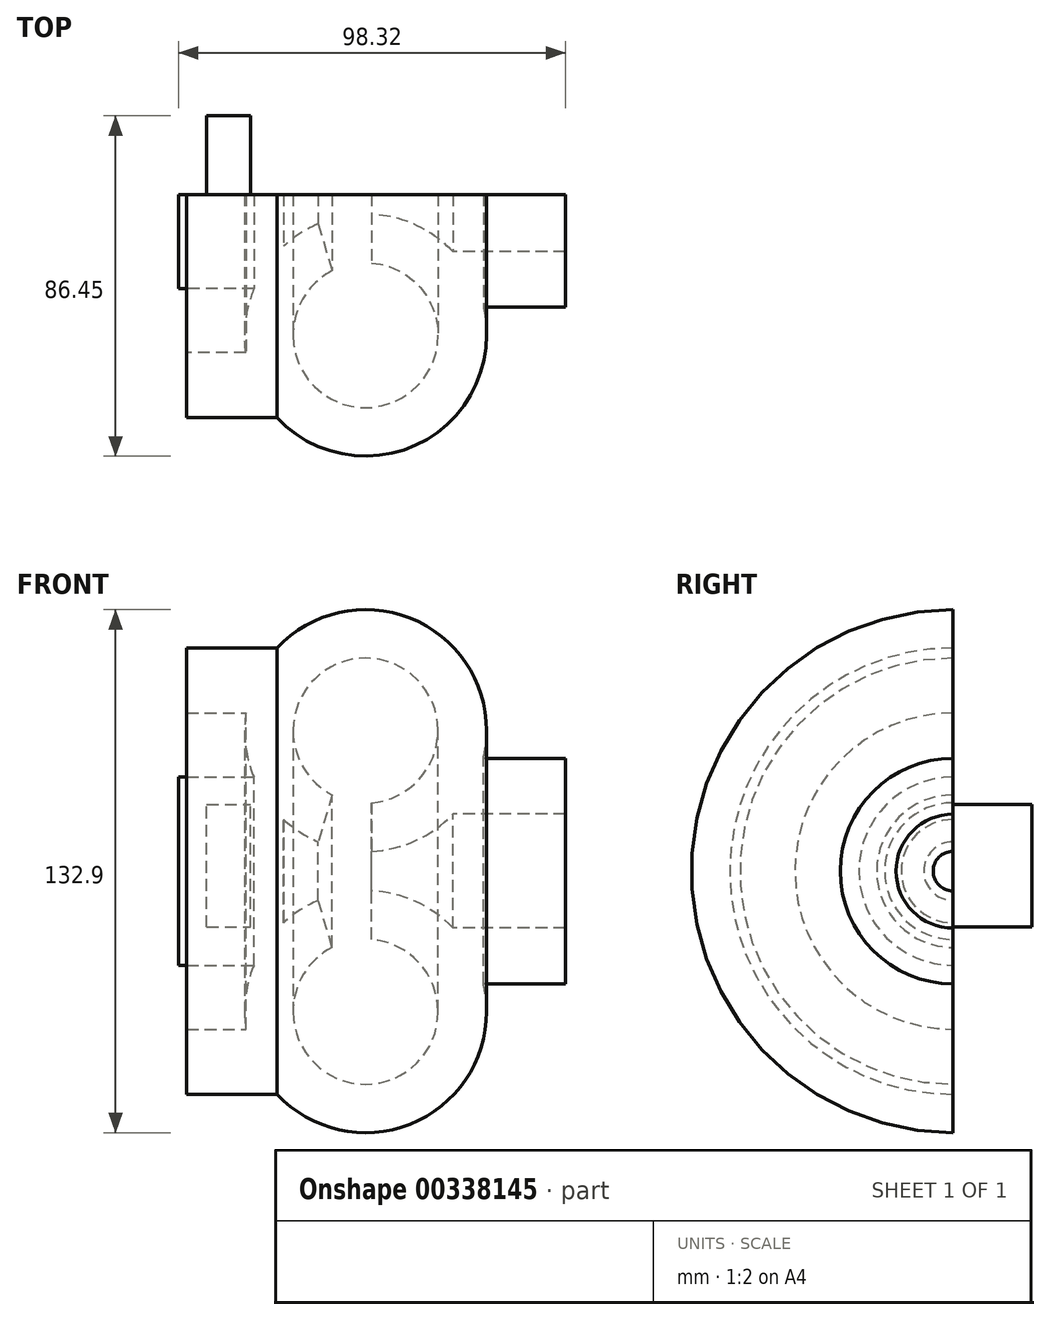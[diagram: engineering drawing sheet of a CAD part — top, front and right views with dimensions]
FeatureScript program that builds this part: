
annotation { "Feature Type Name" : "Feature", "Feature Type Description" : "" }
export const myFeature = defineFeature(function(context is Context, id is Id, definition is map)
    precondition{}
    {
        {
            var Q0;
            Q0=qCreatedBy(makeId("Front.planeOp"),FACE);
            var sketch = newSketch(context, id + "F0", { "sketchPlane" : qUnion([Q0])});
            skArc(sketch, "E0", {"start": v(-9.6, 40.15) * mm, "mid": v(-9.67, 31.9) * mm, "end": v(-7.55, 23.91) * mm});
            skLineSegment(sketch, "E1.bottom", {"start": v(71.6, 14.47) * mm, "end": v(43, 14.47) * mm});
            skLineSegment(sketch, "E1.top", {"start": v(71.6, 28.64) * mm, "end": v(50.71, 28.64) * mm});
            skLineSegment(sketch, "E1.left", {"start": v(71.6, 14.47) * mm, "end": v(71.6, 28.64) * mm});
            skLineSegment(sketch, "E2.bottom", {"start": v(-26.72, 0) * mm, "end": v(0, 0) * mm});
            skLineSegment(sketch, "E2.top", {"start": v(-26.72, 23.91) * mm, "end": v(-7.55, 23.91) * mm});
            skLineSegment(sketch, "E2.left", {"start": v(-26.72, 0) * mm, "end": v(-26.72, 23.91) * mm});
            skLineSegment(sketch, "E2.right", {"start": v(0, 0) * mm, "end": v(0, 13.12) * mm});
            skLineSegment(sketch, "E3.bottom", {"start": v(-24.65, 56.69) * mm, "end": v(-1.65, 56.69) * mm});
            skLineSegment(sketch, "E3.top", {"start": v(-24.65, 40.15) * mm, "end": v(-9.6, 40.15) * mm});
            skLineSegment(sketch, "E3.right", {"start": v(-24.65, 56.69) * mm, "end": v(-24.65, 40.15) * mm});
            skPoint(sketch, "E4.orphan", {"position": v(0, 56.69) * mm});
            skArc(sketch, "E5.trimOffspring", {"start": v(0, 13.12) * mm, "mid": v(4.15, 9.9) * mm, "end": v(8.8, 7.45) * mm});
            skPoint(sketch, "E6.orphan", {"position": v(0, 23.91) * mm});
            skArc(sketch, "E7.trimOffspring", {"start": v(50.71, 28.64) * mm, "mid": v(35.32, 62.81) * mm, "end": v(-1.65, 56.69) * mm});
            skArc(sketch, "E8", {"start": v(22.26, 17.36) * mm, "mid": v(24.48, 53.78) * mm, "end": v(12.33, 19.38) * mm});
            skLineSegment(sketch, "E9", {"start": v(22.26, 17.36) * mm, "end": v(22.26, 5.03) * mm});
            skLineSegment(sketch, "E10", {"start": v(12.33, 19.38) * mm, "end": v(8.8, 7.45) * mm});
            skArc(sketch, "E11.trimOffspring", {"start": v(22.26, 5.03) * mm, "mid": v(33.54, 7.75) * mm, "end": v(43, 14.47) * mm});
            skSolve(sketch);
        }
        {
            var Q0;
            Q0=makeQuery(id+"F0.imprint","IMPRINT",FACE,{"disambiguationData":[TD([[makeQuery(id+"F0.imprint","IMPRINT",EDGE,{"derivedFrom":sQuery(id+"F0.wireOp",EDGE,"E0")}),1.0]])]});
            var Q1;
            Q1=sQuery(id+"F0.wireOp",EDGE,"E2.bottom");
            revolve(context, id + "F1", {"entities" : qUnion([Q0]), "axis" : qUnion([Q1]), "revolveType" : RevolveType.ONE_DIRECTION, "angle" : 180 * degree});
        }
        {
            var Q0;
            Q0=makeQuery(id+"F1.opRevolve","CAP_FACE",FACE,{"disambiguationData":[OSD([sQuery(id+"F0.wireOp",EDGE,"E0"),sQuery(id+"F0.wireOp",EDGE,"E1.bottom"),sQuery(id+"F0.wireOp",EDGE,"E1.top"),sQuery(id+"F0.wireOp",EDGE,"E1.left"),sQuery(id+"F0.wireOp",EDGE,"E2.bottom"),sQuery(id+"F0.wireOp",EDGE,"E2.top"),sQuery(id+"F0.wireOp",EDGE,"E2.left"),sQuery(id+"F0.wireOp",EDGE,"E2.right"),sQuery(id+"F0.wireOp",EDGE,"E3.bottom"),sQuery(id+"F0.wireOp",EDGE,"E3.top"),sQuery(id+"F0.wireOp",EDGE,"E3.right"),sQuery(id+"F0.wireOp",EDGE,"E5.trimOffspring"),sQuery(id+"F0.wireOp",EDGE,"E7.trimOffspring"),sQuery(id+"F0.wireOp",EDGE,"E8"),sQuery(id+"F0.wireOp",EDGE,"E9"),sQuery(id+"F0.wireOp",EDGE,"E10"),sQuery(id+"F0.wireOp",EDGE,"E11.trimOffspring")])],"isStart":false});
            var sketch = newSketch(context, id + "F2", { "sketchPlane" : qUnion([Q0])});
            skLineSegment(sketch, "E12.bottom", {"start": v(19.54, -14.21) * mm, "end": v(8.47, -14.21) * mm});
            skLineSegment(sketch, "E12.top", {"start": v(19.54, 16.98) * mm, "end": v(8.47, 16.98) * mm});
            skLineSegment(sketch, "E12.left", {"start": v(19.54, -14.21) * mm, "end": v(19.54, 16.98) * mm});
            skLineSegment(sketch, "E12.right", {"start": v(8.47, -14.21) * mm, "end": v(8.47, 16.98) * mm});
            skSolve(sketch);
        }
        {
            var Q0;
            Q0 = qSketchRegion(id + "F2", true);
            extrude(context, id + "F3", {"entities" : qUnion([Q0]), "operationType" : NewBodyOperationType.ADD, "depth" : 20 * mm});
        }
    });
